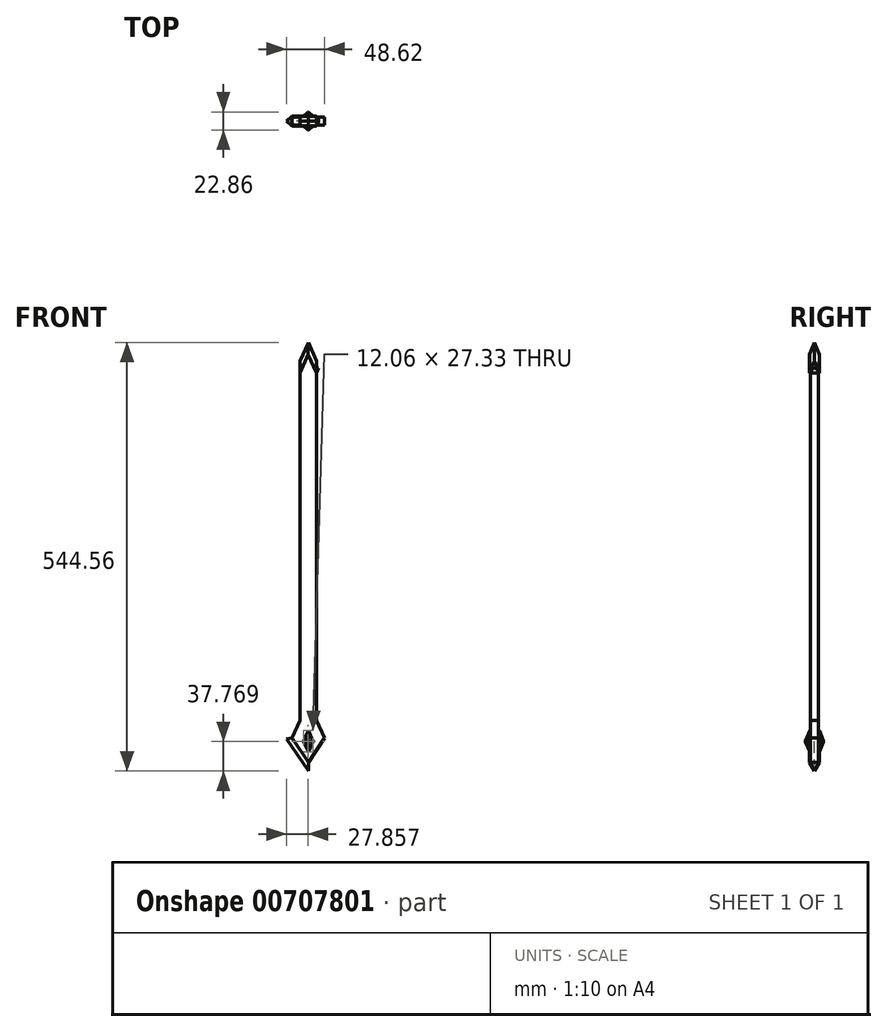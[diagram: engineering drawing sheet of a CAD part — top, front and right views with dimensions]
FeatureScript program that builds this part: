
annotation { "Feature Type Name" : "Feature", "Feature Type Description" : "" }
export const myFeature = defineFeature(function(context is Context, id is Id, definition is map)
    precondition{}
    {
        {
            var Q0;
            Q0=qCreatedBy(makeId("Front.planeOp"),FACE);
            var sketch = newSketch(context, id + "F0", { "sketchPlane" : qUnion([Q0])});
            skLineSegment(sketch, "E0", {"start": v(-27.98, 3.42) * mm, "end": v(0, -37.77) * mm});
            skLineSegment(sketch, "E1", {"start": v(0, -37.77) * mm, "end": v(27.96, 3.42) * mm});
            skLineSegment(sketch, "E2", {"start": v(-27.98, 3.42) * mm, "end": v(-17.14, 28.2) * mm});
            skLineSegment(sketch, "E3", {"start": v(27.96, 3.42) * mm, "end": v(17.08, 28.2) * mm});
            skLineSegment(sketch, "E4", {"start": v(17.08, 28.2) * mm, "end": v(27.96, 3.42) * mm});
            skLineSegment(sketch, "E5", {"start": v(-17.14, 28.2) * mm, "end": v(-17.14, 469.12) * mm});
            skLineSegment(sketch, "E6", {"start": v(-17.14, 469.12) * mm, "end": v(-17.14, 28.2) * mm});
            skLineSegment(sketch, "E7", {"start": v(17.08, 28.2) * mm, "end": v(17.08, 469.12) * mm});
            skLineSegment(sketch, "E8", {"start": v(-17.14, 469.12) * mm, "end": v(0, 506.79) * mm});
            skLineSegment(sketch, "E9", {"start": v(0, 506.79) * mm, "end": v(17.08, 469.12) * mm});
            skSolve(sketch);
        }
        {
            var Q0;
            Q0=makeQuery(id+"F0.imprint","IMPRINT",FACE,{"disambiguationData":[TD([[makeQuery(id+"F0.imprint","IMPRINT",EDGE,{"derivedFrom":sQuery(id+"F0.wireOp",EDGE,"E0")}),1.0]])]});
            extrude(context, id + "F1", {"entities" : qUnion([Q0]), "depth" : 6.35 * mm, "offsetDistance" : 25.4 * mm});
        }
        {
            var Q0;
            Q0=makeQuery(id+"F1.opExtrude","CAP_FACE",FACE,{"disambiguationData":[OSD([sQuery(id+"F0.wireOp",EDGE,"E0"),sQuery(id+"F0.wireOp",EDGE,"E1"),sQuery(id+"F0.wireOp",EDGE,"E2"),sQuery(id+"F0.wireOp",EDGE,"E4"),sQuery(id+"F0.wireOp",EDGE,"E6"),sQuery(id+"F0.wireOp",EDGE,"E7"),sQuery(id+"F0.wireOp",EDGE,"E8"),sQuery(id+"F0.wireOp",EDGE,"E9")])],"isStart":true});
            extrude(context, id + "F2", {"entities" : qUnion([Q0]), "operationType" : NewBodyOperationType.ADD, "depth" : 6.35 * mm, "offsetDistance" : 25.4 * mm});
        }
        {
            var Q0;
            Q0=makeQuery(id+"F1.opExtrude","CAP_FACE",FACE,{"disambiguationData":[OSD([sQuery(id+"F0.wireOp",EDGE,"E0"),sQuery(id+"F0.wireOp",EDGE,"E1"),sQuery(id+"F0.wireOp",EDGE,"E2"),sQuery(id+"F0.wireOp",EDGE,"E4"),sQuery(id+"F0.wireOp",EDGE,"E6"),sQuery(id+"F0.wireOp",EDGE,"E7"),sQuery(id+"F0.wireOp",EDGE,"E8"),sQuery(id+"F0.wireOp",EDGE,"E9")])],"isStart":false});
            var Q1;
            Q1=makeQuery(id+"F2.opExtrude","CAP_FACE",FACE,{"disambiguationData":[OSD([sQuery(id+"F0.wireOp",EDGE,"E0"),sQuery(id+"F0.wireOp",EDGE,"E1"),sQuery(id+"F0.wireOp",EDGE,"E2"),sQuery(id+"F0.wireOp",EDGE,"E4"),sQuery(id+"F0.wireOp",EDGE,"E6"),sQuery(id+"F0.wireOp",EDGE,"E7"),sQuery(id+"F0.wireOp",EDGE,"E8"),sQuery(id+"F0.wireOp",EDGE,"E9")])],"isStart":false});
            chamfer(context, id + "F3", {"entities" : qUnion([Q0, Q1]), "chamferType" : ChamferType.OFFSET_ANGLE, "width" : 6.35 * mm, "oppositeDirection" : false, "angle" : 45 * degree, "tangentPropagation" : true});
        }
        {
            var Q0;
            Q0=makeQuery(id+"F1.opExtrude","CAP_FACE",FACE,{"disambiguationData":[OSD([sQuery(id+"F0.wireOp",EDGE,"E0"),sQuery(id+"F0.wireOp",EDGE,"E1"),sQuery(id+"F0.wireOp",EDGE,"E2"),sQuery(id+"F0.wireOp",EDGE,"E4"),sQuery(id+"F0.wireOp",EDGE,"E6"),sQuery(id+"F0.wireOp",EDGE,"E7"),sQuery(id+"F0.wireOp",EDGE,"E8"),sQuery(id+"F0.wireOp",EDGE,"E9")])],"isStart":false});
            extrude(context, id + "F4", {"entities" : qUnion([Q0]), "operationType" : NewBodyOperationType.ADD, "depth" : 0.03 * mm, "offsetDistance" : 25.4 * mm});
        }
        {
            var Q0;
            Q0=makeQuery(id+"F2.opExtrude","CAP_FACE",FACE,{"disambiguationData":[OSD([sQuery(id+"F0.wireOp",EDGE,"E0"),sQuery(id+"F0.wireOp",EDGE,"E1"),sQuery(id+"F0.wireOp",EDGE,"E2"),sQuery(id+"F0.wireOp",EDGE,"E4"),sQuery(id+"F0.wireOp",EDGE,"E6"),sQuery(id+"F0.wireOp",EDGE,"E7"),sQuery(id+"F0.wireOp",EDGE,"E8"),sQuery(id+"F0.wireOp",EDGE,"E9")])],"isStart":false});
            extrude(context, id + "F5", {"entities" : qUnion([Q0]), "operationType" : NewBodyOperationType.ADD, "depth" : 0.03 * mm, "offsetDistance" : 25.4 * mm});
        }
        {
            var Q0;
            Q0=makeQuery(id+"F4.opExtrude","CAP_FACE",FACE,{"disambiguationData":[OSD([sQuery(id+"F0.wireOp",EDGE,"E0"),sQuery(id+"F0.wireOp",EDGE,"E1"),sQuery(id+"F0.wireOp",EDGE,"E2"),sQuery(id+"F0.wireOp",EDGE,"E4"),sQuery(id+"F0.wireOp",EDGE,"E6"),sQuery(id+"F0.wireOp",EDGE,"E7"),sQuery(id+"F0.wireOp",EDGE,"E8"),sQuery(id+"F0.wireOp",EDGE,"E9")])],"isStart":false});
            var sketch = newSketch(context, id + "F6", { "sketchPlane" : qUnion([Q0])});
            skLineSegment(sketch, "E10.bottom", {"start": v(10.73, 99.07) * mm, "end": v(32.7, 99.07) * mm});
            skLineSegment(sketch, "E10.top", {"start": v(10.73, 29.55) * mm, "end": v(32.7, 29.55) * mm});
            skLineSegment(sketch, "E10.left", {"start": v(10.73, 99.07) * mm, "end": v(10.73, 29.55) * mm});
            skLineSegment(sketch, "E10.right", {"start": v(32.7, 99.07) * mm, "end": v(32.7, 29.55) * mm});
            skLineSegment(sketch, "E11", {"start": v(10.73, 29.55) * mm, "end": v(10.73, 26.86) * mm});
            skLineSegment(sketch, "E12", {"start": v(10.73, 26.86) * mm, "end": v(24.63, -4.77) * mm});
            skLineSegment(sketch, "E13", {"start": v(24.63, -4.77) * mm, "end": v(32.22, 4.08) * mm});
            skLineSegment(sketch, "E14", {"start": v(32.22, 4.08) * mm, "end": v(20.74, 31.63) * mm});
            skLineSegment(sketch, "E15", {"start": v(20.74, 31.63) * mm, "end": v(10.73, 29.55) * mm});
            skLineSegment(sketch, "E16", {"start": v(20.74, 4.08) * mm, "end": v(29.74, -3.64) * mm});
            skLineSegment(sketch, "E17", {"start": v(29.74, -3.64) * mm, "end": v(0, -41.62) * mm});
            skLineSegment(sketch, "E18", {"start": v(0, -41.62) * mm, "end": v(0, -26.47) * mm});
            skLineSegment(sketch, "E19", {"start": v(0, -26.47) * mm, "end": v(0, -41.62) * mm});
            skLineSegment(sketch, "E20", {"start": v(0, -41.62) * mm, "end": v(-30.32, 3) * mm});
            skLineSegment(sketch, "E21", {"start": v(-30.32, 3) * mm, "end": v(-20.76, 4.09) * mm});
            skLineSegment(sketch, "E22", {"start": v(-20.76, 4.09) * mm, "end": v(0, -26.47) * mm});
            skLineSegment(sketch, "E23", {"start": v(-30.32, 3) * mm, "end": v(-18.35, 33.11) * mm});
            skLineSegment(sketch, "E24", {"start": v(-18.35, 33.11) * mm, "end": v(-10.79, 26.87) * mm});
            skLineSegment(sketch, "E25", {"start": v(-10.79, 26.87) * mm, "end": v(-20.76, 4.09) * mm});
            skLineSegment(sketch, "E26.bottom", {"start": v(-10.79, 26.87) * mm, "end": v(-21.72, 26.87) * mm});
            skLineSegment(sketch, "E26.top", {"start": v(-10.79, 486.68) * mm, "end": v(-21.72, 486.68) * mm});
            skLineSegment(sketch, "E26.left", {"start": v(-10.79, 26.87) * mm, "end": v(-10.79, 486.68) * mm});
            skLineSegment(sketch, "E26.right", {"start": v(-21.72, 26.87) * mm, "end": v(-21.72, 486.68) * mm});
            skLineSegment(sketch, "E27.bottom", {"start": v(32.7, 29.55) * mm, "end": v(10.73, 29.55) * mm});
            skLineSegment(sketch, "E27.top", {"start": v(32.7, 505.5) * mm, "end": v(10.73, 505.5) * mm});
            skLineSegment(sketch, "E27.left", {"start": v(32.7, 29.55) * mm, "end": v(32.7, 505.5) * mm});
            skLineSegment(sketch, "E27.right", {"start": v(10.73, 29.55) * mm, "end": v(10.73, 505.5) * mm});
            skLineSegment(sketch, "E28.bottom", {"start": v(10.73, 467.75) * mm, "end": v(20.74, 467.75) * mm});
            skLineSegment(sketch, "E28.top", {"start": v(10.73, 474.1) * mm, "end": v(20.74, 474.1) * mm});
            skLineSegment(sketch, "E28.left", {"start": v(10.73, 467.75) * mm, "end": v(10.73, 474.1) * mm});
            skLineSegment(sketch, "E28.right", {"start": v(20.74, 467.75) * mm, "end": v(20.74, 474.1) * mm});
            skLineSegment(sketch, "E29", {"start": v(10.73, 467.75) * mm, "end": v(19.45, 491.03) * mm});
            skLineSegment(sketch, "E30", {"start": v(19.45, 491.03) * mm, "end": v(0, 514.64) * mm});
            skLineSegment(sketch, "E31", {"start": v(0, 514.64) * mm, "end": v(-16.26, 476.1) * mm});
            skPoint(sketch, "E31.endSnap0", {"position": v(-16.26, 486.68) * mm});
            skLineSegment(sketch, "E32", {"start": v(-16.26, 476.1) * mm, "end": v(-10.79, 467.75) * mm});
            skSolve(sketch);
        }
        {
            var Q0;
            {var subQ0=sQuery(id+"F6.wireOp",EDGE,"E28.left");Q0=makeQuery(id+"F6.imprint","IMPRINT",FACE,{"disambiguationData":[TD([[makeQuery(id+"F6.imprint","IMPRINT",EDGE,{"derivedFrom":subQ0}),1.0]])]});}
            var Q1;
            {var subQ5=sQuery(id+"F6.wireOp",EDGE,"E32");Q1=makeQuery(id+"F6.imprint","IMPRINT",FACE,{"disambiguationData":[TD([[makeQuery(id+"F6.imprint","IMPRINT",EDGE,{"derivedFrom":subQ5}),1.0]])]});}
            var Q2;
            {var subQ7=sQuery(id+"F6.wireOp",EDGE,"E24");Q2=makeQuery(id+"F6.imprint","IMPRINT",FACE,{"disambiguationData":[TD([[makeQuery(id+"F6.imprint","IMPRINT",EDGE,{"derivedFrom":subQ7}),1.0]])]});}
            var Q3;
            {var subQ3=sQuery(id+"F6.wireOp",EDGE,"E30");var subQ5=sQuery(id+"F6.wireOp",EDGE,"E29");var subQ7=makeQuery(id+"F6.imprint","INTERSECT",VERTEX,{"derivedFrom":[subQ5,subQ3]});Q3=makeQuery(id+"F6.imprint","IMPRINT",FACE,{"disambiguationData":[TD([[makeQuery(id+"F6.imprint","IMPRINT",EDGE,{"disambiguationData":[TD([[subQ7,1.0]])],"derivedFrom":subQ5}),1.0]])]});}
            var Q4;
            {var subQ11=sQuery(id+"F6.wireOp",EDGE,"E10.bottom");Q4=makeQuery(id+"F6.imprint","IMPRINT",FACE,{"disambiguationData":[TD([[makeQuery(id+"F6.imprint","IMPRINT",EDGE,{"derivedFrom":subQ11}),1.0]])]});}
            var Q5;
            {var subQ0=sQuery(id+"F6.wireOp",EDGE,"E28.bottom");Q5=makeQuery(id+"F6.imprint","IMPRINT",FACE,{"disambiguationData":[TD([[makeQuery(id+"F6.imprint","IMPRINT",EDGE,{"derivedFrom":subQ0}),1.0]])]});}
            var Q6;
            {var subQ0=sQuery(id+"F6.wireOp",EDGE,"E28.left");Q6=makeQuery(id+"F6.imprint","IMPRINT",FACE,{"disambiguationData":[TD([[makeQuery(id+"F6.imprint","IMPRINT",EDGE,{"derivedFrom":subQ0}),-1.0]])]});}
            var Q7;
            {var subQ2=sQuery(id+"F6.wireOp",EDGE,"E10.bottom");Q7=makeQuery(id+"F6.imprint","IMPRINT",FACE,{"disambiguationData":[TD([[makeQuery(id+"F6.imprint","IMPRINT",EDGE,{"derivedFrom":subQ2}),-1.0]])]});}
            var Q8;
            {var subQ0=sQuery(id+"F6.wireOp",EDGE,"E24");Q8=makeQuery(id+"F6.imprint","IMPRINT",FACE,{"disambiguationData":[TD([[makeQuery(id+"F6.imprint","IMPRINT",EDGE,{"derivedFrom":subQ0}),-1.0]])]});}
            var Q9;
            {var subQ15=sQuery(id+"F6.wireOp",EDGE,"E11");Q9=makeQuery(id+"F6.imprint","IMPRINT",FACE,{"disambiguationData":[TD([[makeQuery(id+"F6.imprint","IMPRINT",EDGE,{"derivedFrom":subQ15}),-1.0]])]});}
            var Q10;
            {var subQ0=sQuery(id+"F6.wireOp",EDGE,"E21");Q10=makeQuery(id+"F6.imprint","IMPRINT",FACE,{"disambiguationData":[TD([[makeQuery(id+"F6.imprint","IMPRINT",EDGE,{"derivedFrom":subQ0}),1.0]])]});}
            var Q11;
            {var subQ0=sQuery(id+"F6.wireOp",EDGE,"E17");Q11=makeQuery(id+"F6.imprint","IMPRINT",FACE,{"disambiguationData":[TD([[makeQuery(id+"F6.imprint","IMPRINT",EDGE,{"derivedFrom":subQ0}),-1.0]])]});}
            var Q12;
            {var subQ1=sQuery(id+"F6.wireOp",EDGE,"E12");var subQ11=sQuery(id+"F6.wireOp",EDGE,"E13");var subQ12=makeQuery(id+"F6.imprint","INTERSECT",VERTEX,{"derivedFrom":[subQ1,subQ11]});Q12=makeQuery(id+"F6.imprint","IMPRINT",FACE,{"disambiguationData":[TD([[makeQuery(id+"F6.imprint","IMPRINT",EDGE,{"disambiguationData":[TD([[subQ12,-1.0]])],"derivedFrom":subQ11}),1.0]])]});}
            var Q13;
            {var subQ0=sQuery(id+"F6.wireOp",EDGE,"E15");Q13=makeQuery(id+"F6.imprint","IMPRINT",FACE,{"disambiguationData":[TD([[makeQuery(id+"F6.imprint","IMPRINT",EDGE,{"derivedFrom":subQ0}),1.0]])]});}
            var Q14;
            Q14=makeQuery(id+"F6.imprint","IMPRINT",FACE,{"disambiguationData":[TD([[makeQuery(id+"F6.imprint","IMPRINT",EDGE,{"derivedFrom":sQuery(id+"F6.wireOp",EDGE,"E19")}),-1.0]])]});
            extrude(context, id + "F7", {"entities" : qUnion([Q0, Q1, Q2, Q3, Q4, Q5, Q6, Q7, Q8, Q9, Q10, Q11, Q12, Q13, Q14]), "operationType" : NewBodyOperationType.REMOVE, "oppositeDirection" : true, "depth" : 25.4 * mm, "offsetDistance" : 25.4 * mm});
        }
        {
            var Q0;
            Q0=makeQuery(id+"F4.opExtrude","CAP_FACE",FACE,{"disambiguationData":[OSD([sQuery(id+"F0.wireOp",EDGE,"E0"),sQuery(id+"F0.wireOp",EDGE,"E1"),sQuery(id+"F0.wireOp",EDGE,"E2"),sQuery(id+"F0.wireOp",EDGE,"E4"),sQuery(id+"F0.wireOp",EDGE,"E6"),sQuery(id+"F0.wireOp",EDGE,"E7"),sQuery(id+"F0.wireOp",EDGE,"E8"),sQuery(id+"F0.wireOp",EDGE,"E9")])],"isStart":false});
            extrude(context, id + "F8", {"entities" : qUnion([Q0]), "operationType" : NewBodyOperationType.REMOVE, "oppositeDirection" : true, "depth" : 0.03 * mm, "offsetDistance" : 25.4 * mm});
        }
        {
            var Q0;
            Q0=makeQuery(id+"F5.opExtrude","CAP_FACE",FACE,{"disambiguationData":[OSD([sQuery(id+"F0.wireOp",EDGE,"E0"),sQuery(id+"F0.wireOp",EDGE,"E1"),sQuery(id+"F0.wireOp",EDGE,"E2"),sQuery(id+"F0.wireOp",EDGE,"E4"),sQuery(id+"F0.wireOp",EDGE,"E6"),sQuery(id+"F0.wireOp",EDGE,"E7"),sQuery(id+"F0.wireOp",EDGE,"E8"),sQuery(id+"F0.wireOp",EDGE,"E9")])],"isStart":false});
            extrude(context, id + "F9", {"entities" : qUnion([Q0]), "operationType" : NewBodyOperationType.REMOVE, "oppositeDirection" : true, "depth" : 0.03 * mm, "offsetDistance" : 25.4 * mm});
        }
        {
            var Q0;
            Q0=makeQuery(id+"F8.boolean.opBoolean","COPY",FACE,{"derivedFrom":makeQuery(id+"F8.opExtrude","CAP_FACE",FACE,{"disambiguationData":[OSD([sQuery(id+"F0.wireOp",EDGE,"E0"),sQuery(id+"F0.wireOp",EDGE,"E1"),sQuery(id+"F0.wireOp",EDGE,"E2"),sQuery(id+"F0.wireOp",EDGE,"E4"),sQuery(id+"F0.wireOp",EDGE,"E6"),sQuery(id+"F0.wireOp",EDGE,"E7"),sQuery(id+"F0.wireOp",EDGE,"E8"),sQuery(id+"F0.wireOp",EDGE,"E9")])],"isStart":false})});
            extrude(context, id + "F10", {"entities" : qUnion([Q0]), "operationType" : NewBodyOperationType.REMOVE, "oppositeDirection" : true, "depth" : 1.27 * mm, "offsetDistance" : 25.4 * mm});
        }
        {
            var Q0;
            Q0=makeQuery(id+"F9.boolean.opBoolean","COPY",FACE,{"derivedFrom":makeQuery(id+"F9.opExtrude","CAP_FACE",FACE,{"disambiguationData":[OSD([sQuery(id+"F0.wireOp",EDGE,"E0"),sQuery(id+"F0.wireOp",EDGE,"E1"),sQuery(id+"F0.wireOp",EDGE,"E2"),sQuery(id+"F0.wireOp",EDGE,"E4"),sQuery(id+"F0.wireOp",EDGE,"E6"),sQuery(id+"F0.wireOp",EDGE,"E7"),sQuery(id+"F0.wireOp",EDGE,"E8"),sQuery(id+"F0.wireOp",EDGE,"E9")])],"isStart":false})});
            extrude(context, id + "F11", {"entities" : qUnion([Q0]), "operationType" : NewBodyOperationType.REMOVE, "oppositeDirection" : true, "depth" : 1.27 * mm, "offsetDistance" : 25.4 * mm});
        }
        {
            var Q0;
            Q0=makeQuery(id+"F11.boolean.opBoolean","COPY",FACE,{"derivedFrom":makeQuery(id+"F11.opExtrude","CAP_FACE",FACE,{"disambiguationData":[OSD([sQuery(id+"F0.wireOp",EDGE,"E0"),sQuery(id+"F0.wireOp",EDGE,"E1"),sQuery(id+"F0.wireOp",EDGE,"E2"),sQuery(id+"F0.wireOp",EDGE,"E4"),sQuery(id+"F0.wireOp",EDGE,"E6"),sQuery(id+"F0.wireOp",EDGE,"E7"),sQuery(id+"F0.wireOp",EDGE,"E8"),sQuery(id+"F0.wireOp",EDGE,"E9")])],"isStart":false})});
            var sketch = newSketch(context, id + "F12", { "sketchPlane" : qUnion([Q0])});
            skLineSegment(sketch, "E33", {"start": v(0, 13.66) * mm, "end": v(-6, 0) * mm});
            skLineSegment(sketch, "E34", {"start": v(-6, 0) * mm, "end": v(0, -13.67) * mm});
            skLineSegment(sketch, "E35", {"start": v(0, -13.67) * mm, "end": v(6.05, 0) * mm});
            skLineSegment(sketch, "E36", {"start": v(6.05, 0) * mm, "end": v(0, 13.66) * mm});
            skSolve(sketch);
        }
        {
            var Q0;
            Q0=makeQuery(id+"F12.imprint","IMPRINT",FACE,{"disambiguationData":[TD([[makeQuery(id+"F12.imprint","IMPRINT",EDGE,{"derivedFrom":sQuery(id+"F12.wireOp",EDGE,"E33")}),1.0]])]});
            extrude(context, id + "F13", {"entities" : qUnion([Q0]), "operationType" : NewBodyOperationType.ADD, "depth" : 6.35 * mm, "offsetDistance" : 25.4 * mm});
        }
        {
            var Q0;
            Q0=makeQuery(id+"F13.opExtrude","CAP_FACE",FACE,{"disambiguationData":[OSD([sQuery(id+"F12.wireOp",EDGE,"E33"),sQuery(id+"F12.wireOp",EDGE,"E34"),sQuery(id+"F12.wireOp",EDGE,"E35"),sQuery(id+"F12.wireOp",EDGE,"E36")])],"isStart":false});
            extrude(context, id + "F14", {"entities" : qUnion([Q0]), "operationType" : NewBodyOperationType.ADD, "oppositeDirection" : true, "depth" : 22.86 * mm, "offsetDistance" : 25.4 * mm});
        }
        {
            var Q0;
            Q0=makeQuery(id+"F13.opExtrude","CAP_FACE",FACE,{"disambiguationData":[OSD([sQuery(id+"F12.wireOp",EDGE,"E33"),sQuery(id+"F12.wireOp",EDGE,"E34"),sQuery(id+"F12.wireOp",EDGE,"E35"),sQuery(id+"F12.wireOp",EDGE,"E36")])],"isStart":false});
            var Q1;
            Q1=makeQuery(id+"F14.opExtrude","CAP_FACE",FACE,{"disambiguationData":[OSD([sQuery(id+"F12.wireOp",EDGE,"E33"),sQuery(id+"F12.wireOp",EDGE,"E34"),sQuery(id+"F12.wireOp",EDGE,"E35"),sQuery(id+"F12.wireOp",EDGE,"E36")])],"isStart":false});
            chamfer(context, id + "F15", {"entities" : qUnion([Q0, Q1]), "width" : 5.33 * mm, "tangentPropagation" : true});
        }
    });
